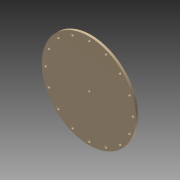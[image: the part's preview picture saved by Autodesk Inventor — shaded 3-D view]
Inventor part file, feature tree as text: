
AUTODESK INVENTOR PART (.ipt)
format: ipt  version: 2013 (Build 170138000, 138)  size: 101,888 bytes
history: native  units: in
note: dims shown in document units (in); Inventor stores cm internally (conversion verified against a paired STEP export)
features: sketch x3, hole x2, extrude x1, pattern_circular x1
ambient origin geometry x8: Origin, YZ Plane, XZ Plane, XY Plane, X Axis, Y Axis, Z Axis, Center Point
bodies: Solid1 (feature_tree)
feature tree (7):
  extrude  "Extrusion1"  Depth=10.0in
  hole  "Hole1"  [1 undecoded]
  hole  "Hole2"  [1 undecoded]
  pattern_circular  "Circular Pattern1"  [2 undecoded]
  sketch  "Sketch1"  dims[d0=0.25in d1=0.0in d2=10.0in]
  sketch  "Sketch2"  dims[d4=0.27in d5=0.75in d6=0.375in d7=0.25in d8=0.5635in d9=1.0in d10=0.8108in d11=9.25in]
  sketch  "Sketch3"  dims[d13=0.31in d14=0.75in d15=0.375in d16=0.25in d17=0.5635in d18=1.0in d19=0.8108in d20=6.2992in d21=360.0deg]
note: 4 required parameter values undecoded (feature->parameter linkage not recoverable at this tier; creation-order binding heuristic only, values carry confidence <= 0.55)
